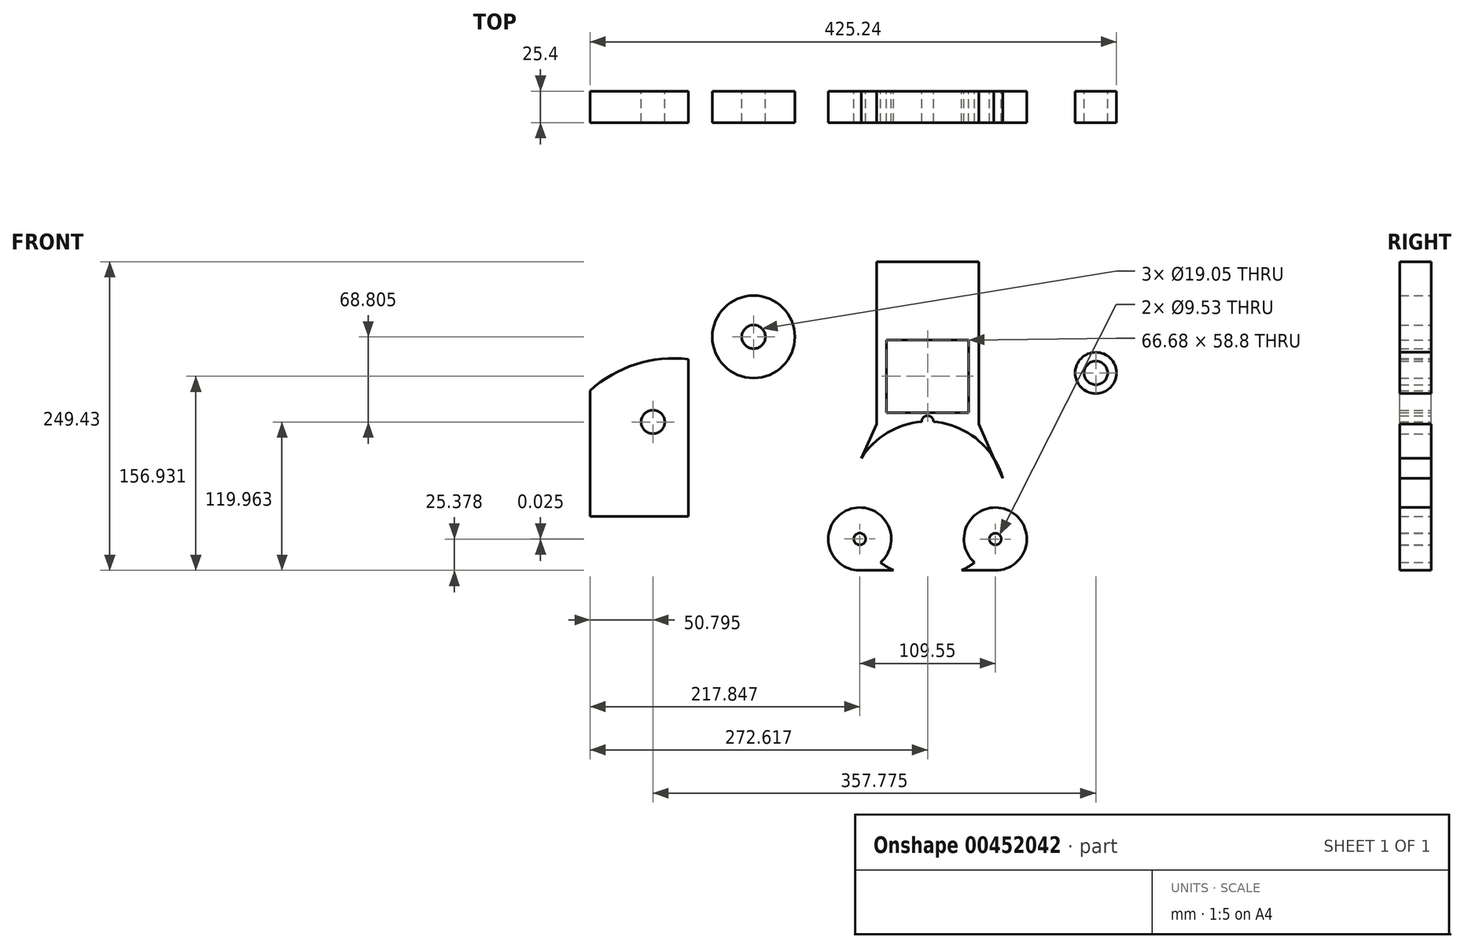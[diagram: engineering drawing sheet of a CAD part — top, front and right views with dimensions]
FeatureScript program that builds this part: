
annotation { "Feature Type Name" : "Feature", "Feature Type Description" : "" }
export const myFeature = defineFeature(function(context is Context, id is Id, definition is map)
    precondition{}
    {
        {
            var Q0;
            Q0=qCreatedBy(makeId("Front.planeOp"),FACE);
            var sketch = newSketch(context, id + "F0", { "sketchPlane" : qUnion([Q0])});
            skCircle(sketch, "E0", {"center": v(0, 0) * mm, "radius": 63.25 * mm});
            skCircle(sketch, "E1", {"center": v(0, 63.25) * mm, "radius": 4.76 * mm});
            skCircle(sketch, "E2", {"center": v(54.77, -31.63) * mm, "radius": 4.76 * mm});
            skCircle(sketch, "E3", {"center": v(-54.78, -31.6) * mm, "radius": 4.76 * mm});
            skLineSegment(sketch, "E4.bottom", {"start": v(-33.35, 70.52) * mm, "end": v(33.32, 70.52) * mm});
            skLineSegment(sketch, "E4.top", {"start": v(-33.35, 129.32) * mm, "end": v(33.32, 129.32) * mm});
            skLineSegment(sketch, "E4.left", {"start": v(-33.35, 70.52) * mm, "end": v(-33.35, 129.32) * mm});
            skLineSegment(sketch, "E4.right", {"start": v(33.32, 70.52) * mm, "end": v(33.32, 129.32) * mm});
            skLineSegment(sketch, "E5", {"start": v(-41.28, 192.42) * mm, "end": v(41.27, 192.42) * mm});
            skLineSegment(sketch, "E6", {"start": v(-41.28, 192.42) * mm, "end": v(-41.27, 61.27) * mm});
            skLineSegment(sketch, "E7", {"start": v(41.28, 192.42) * mm, "end": v(41.28, 61.27) * mm});
            skCircle(sketch, "E8", {"center": v(-54.78, -31.6) * mm, "radius": 25.4 * mm});
            skLineSegment(sketch, "E9", {"start": v(-41.28, 61.27) * mm, "end": v(-78, -21.28) * mm});
            skLineSegment(sketch, "E10", {"start": v(-54.78, -57) * mm, "end": v(54.78, -57) * mm});
            skLineSegment(sketch, "E11.MirrorCS", {"start": v(41.28, 61.27) * mm, "end": v(78, -21.28) * mm});
            skCircle(sketch, "E12.MirrorC", {"center": v(54.78, -31.6) * mm, "radius": 25.4 * mm});
            skSolve(sketch);
        }
        {
            var Q0;
            Q0=qCreatedBy(makeId("Front.planeOp"),FACE);
            var sketch = newSketch(context, id + "F1", { "sketchPlane" : qUnion([Q0])});
            skLineSegment(sketch, "E13", {"start": v(-272.63, -13.25) * mm, "end": v(-193.26, -13.25) * mm});
            skLineSegment(sketch, "E14", {"start": v(-193.26, -13.25) * mm, "end": v(-193.26, 113.75) * mm});
            skCircle(sketch, "E15", {"center": v(-221.83, 62.95) * mm, "radius": 9.53 * mm});
            skArc(sketch, "E16", {"start": v(-193.26, 113.75) * mm, "mid": v(-235.67, 109.57) * mm, "end": v(-272.63, 88.35) * mm});
            skLineSegment(sketch, "E17", {"start": v(-272.63, 88.35) * mm, "end": v(-272.63, -13.25) * mm});
            skSolve(sketch);
        }
        {
            var Q0;
            Q0=makeQuery(id+"F1.imprint","IMPRINT",FACE,{"disambiguationData":[TD([[makeQuery(id+"F1.imprint","IMPRINT",EDGE,{"derivedFrom":sQuery(id+"F1.wireOp",EDGE,"E13")}),1.0]])]});
            extrude(context, id + "F2", {"entities" : qUnion([Q0]), "depth" : 25.4 * mm});
        }
        {
            var Q0;
            Q0=qCreatedBy(makeId("Front.planeOp"),FACE);
            var sketch = newSketch(context, id + "F3", { "sketchPlane" : qUnion([Q0])});
            skCircle(sketch, "E18", {"center": v(-140.56, 131.76) * mm, "radius": 9.53 * mm});
            skCircle(sketch, "E19", {"center": v(-140.56, 131.76) * mm, "radius": 33.34 * mm});
            skLineSegment(sketch, "E20", {"start": v(-140.56, 182.56) * mm, "end": v(-173.9, 182.56) * mm});
            skLineSegment(sketch, "E21", {"start": v(-173.9, 182.56) * mm, "end": v(-107.23, 182.56) * mm});
            skLineSegment(sketch, "E22", {"start": v(-107.23, 182.56) * mm, "end": v(-107.22, 131.76) * mm});
            skLineSegment(sketch, "E23", {"start": v(-173.9, 182.56) * mm, "end": v(-173.9, 131.75) * mm});
            skSolve(sketch);
        }
        {
            var Q0;
            {var subQ0=sQuery(id+"F3.wireOp",EDGE,"E22");Q0=makeQuery(id+"F3.imprint","IMPRINT",FACE,{"disambiguationData":[TD([[makeQuery(id+"F3.imprint","IMPRINT",EDGE,{"derivedFrom":subQ0}),-1.0]])]});}
            var Q1;
            Q1=makeQuery(id+"F3.imprint","IMPRINT",FACE,{"disambiguationData":[TD([[makeQuery(id+"F3.imprint","IMPRINT",EDGE,{"derivedFrom":sQuery(id+"F3.wireOp",EDGE,"E18")}),-1.0]])]});
            extrude(context, id + "F4", {"entities" : qUnion([Q0, Q1]), "depth" : 25.4 * mm});
        }
        {
            var Q0;
            Q0=makeQuery(id+"F0.imprint","IMPRINT",FACE,{"disambiguationData":[TD([[makeQuery(id+"F0.imprint","IMPRINT",EDGE,{"derivedFrom":sQuery(id+"F0.wireOp",EDGE,"E4.bottom")}),-1.0]])]});
            var Q1;
            {var subQ1=sQuery(id+"F0.wireOp",EDGE,"E0");var subQ7=sQuery(id+"F0.wireOp",EDGE,"E11.MirrorCS");var subQ15=makeQuery(id+"F0.imprint","INTERSECT",VERTEX,{"disambiguationData":[OD(0.0)],"derivedFrom":[subQ1,subQ7]});Q1=makeQuery(id+"F0.imprint","IMPRINT",FACE,{"disambiguationData":[TD([[makeQuery(id+"F0.imprint","IMPRINT",EDGE,{"disambiguationData":[TD([[subQ15,-1.0]])],"derivedFrom":subQ1}),1.0]])]});}
            var Q2;
            {var subQ0=sQuery(id+"F0.wireOp",EDGE,"E8");var subQ1=sQuery(id+"F0.wireOp",EDGE,"E0");var subQ2=makeQuery(id+"F0.imprint","INTERSECT",VERTEX,{"disambiguationData":[OD(0.0)],"derivedFrom":[subQ1,subQ0]});Q2=makeQuery(id+"F0.imprint","IMPRINT",FACE,{"disambiguationData":[TD([[makeQuery(id+"F0.imprint","IMPRINT",EDGE,{"disambiguationData":[TD([[subQ2,-1.0]])],"derivedFrom":subQ1}),1.0]])]});}
            var Q3;
            {var subQ0=sQuery(id+"F0.wireOp",EDGE,"E12.MirrorC");var subQ1=sQuery(id+"F0.wireOp",EDGE,"E0");var subQ2=makeQuery(id+"F0.imprint","INTERSECT",VERTEX,{"disambiguationData":[OD(0.0)],"derivedFrom":[subQ1,subQ0]});Q3=makeQuery(id+"F0.imprint","IMPRINT",FACE,{"disambiguationData":[TD([[makeQuery(id+"F0.imprint","IMPRINT",EDGE,{"disambiguationData":[TD([[subQ2,-1.0]])],"derivedFrom":subQ1}),1.0]])]});}
            var Q4;
            {var subQ0=sQuery(id+"F0.wireOp",EDGE,"E11.MirrorCS");var subQ1=sQuery(id+"F0.wireOp",EDGE,"E0");var subQ2=makeQuery(id+"F0.imprint","INTERSECT",VERTEX,{"disambiguationData":[OD(1.0)],"derivedFrom":[subQ1,subQ0]});Q4=makeQuery(id+"F0.imprint","IMPRINT",FACE,{"disambiguationData":[TD([[makeQuery(id+"F0.imprint","IMPRINT",EDGE,{"disambiguationData":[TD([[subQ2,1.0]])],"derivedFrom":subQ1}),-1.0]])]});}
            var Q5;
            {var subQ1=sQuery(id+"F0.wireOp",EDGE,"E0");var subQ4=sQuery(id+"F0.wireOp",EDGE,"E12.MirrorC");var subQ7=makeQuery(id+"F0.imprint","INTERSECT",VERTEX,{"disambiguationData":[OD(0.0)],"derivedFrom":[subQ1,subQ4]});Q5=makeQuery(id+"F0.imprint","IMPRINT",FACE,{"disambiguationData":[TD([[makeQuery(id+"F0.imprint","IMPRINT",EDGE,{"disambiguationData":[TD([[subQ7,-1.0]])],"derivedFrom":subQ1}),-1.0]])]});}
            var Q6;
            {var subQ0=sQuery(id+"F0.wireOp",EDGE,"E8");var subQ2=sQuery(id+"F0.wireOp",EDGE,"E0");var subQ3=makeQuery(id+"F0.imprint","INTERSECT",VERTEX,{"disambiguationData":[OD(0.0)],"derivedFrom":[subQ2,subQ0]});Q6=makeQuery(id+"F0.imprint","IMPRINT",FACE,{"disambiguationData":[TD([[makeQuery(id+"F0.imprint","IMPRINT",EDGE,{"disambiguationData":[TD([[subQ3,-1.0]])],"derivedFrom":subQ2}),-1.0]])]});}
            var Q7;
            {var subQ0=sQuery(id+"F0.wireOp",EDGE,"E9");var subQ1=sQuery(id+"F0.wireOp",EDGE,"E0");var subQ2=makeQuery(id+"F0.imprint","INTERSECT",VERTEX,{"disambiguationData":[OD(1.0)],"derivedFrom":[subQ1,subQ0]});Q7=makeQuery(id+"F0.imprint","IMPRINT",FACE,{"disambiguationData":[TD([[makeQuery(id+"F0.imprint","IMPRINT",EDGE,{"disambiguationData":[TD([[subQ2,-1.0]])],"derivedFrom":subQ1}),-1.0]])]});}
            var Q8;
            {var subQ0=sQuery(id+"F0.wireOp",EDGE,"E10");var subQ1=sQuery(id+"F0.wireOp",EDGE,"E0");var subQ2=makeQuery(id+"F0.imprint","INTERSECT",VERTEX,{"disambiguationData":[OD(0.0)],"derivedFrom":[subQ1,subQ0]});Q8=makeQuery(id+"F0.imprint","IMPRINT",FACE,{"disambiguationData":[TD([[makeQuery(id+"F0.imprint","IMPRINT",EDGE,{"disambiguationData":[TD([[subQ2,1.0]])],"derivedFrom":subQ1}),-1.0]])]});}
            var Q9;
            {var subQ0=sQuery(id+"F0.wireOp",EDGE,"E10");var subQ1=sQuery(id+"F0.wireOp",EDGE,"E0");var subQ2=makeQuery(id+"F0.imprint","INTERSECT",VERTEX,{"disambiguationData":[OD(1.0)],"derivedFrom":[subQ1,subQ0]});Q9=makeQuery(id+"F0.imprint","IMPRINT",FACE,{"disambiguationData":[TD([[makeQuery(id+"F0.imprint","IMPRINT",EDGE,{"disambiguationData":[TD([[subQ2,-1.0]])],"derivedFrom":subQ1}),-1.0]])]});}
            extrude(context, id + "F5", {"entities" : qUnion([Q0, Q1, Q2, Q3, Q4, Q5, Q6, Q7, Q8, Q9]), "depth" : 25.4 * mm});
        }
        {
            var Q0;
            Q0=qCreatedBy(makeId("Front.planeOp"),FACE);
            var sketch = newSketch(context, id + "F6", { "sketchPlane" : qUnion([Q0])});
            skCircle(sketch, "E24", {"center": v(135.94, 102.58) * mm, "radius": 16.67 * mm});
            skCircle(sketch, "E25", {"center": v(135.94, 102.58) * mm, "radius": 9.53 * mm});
            skSolve(sketch);
        }
        {
            var Q0;
            Q0=makeQuery(id+"F6.imprint","IMPRINT",FACE,{"disambiguationData":[TD([[makeQuery(id+"F6.imprint","IMPRINT",EDGE,{"derivedFrom":sQuery(id+"F6.wireOp",EDGE,"E24")}),1.0]])]});
            extrude(context, id + "F7", {"entities" : qUnion([Q0]), "depth" : 25.4 * mm});
        }
    });
